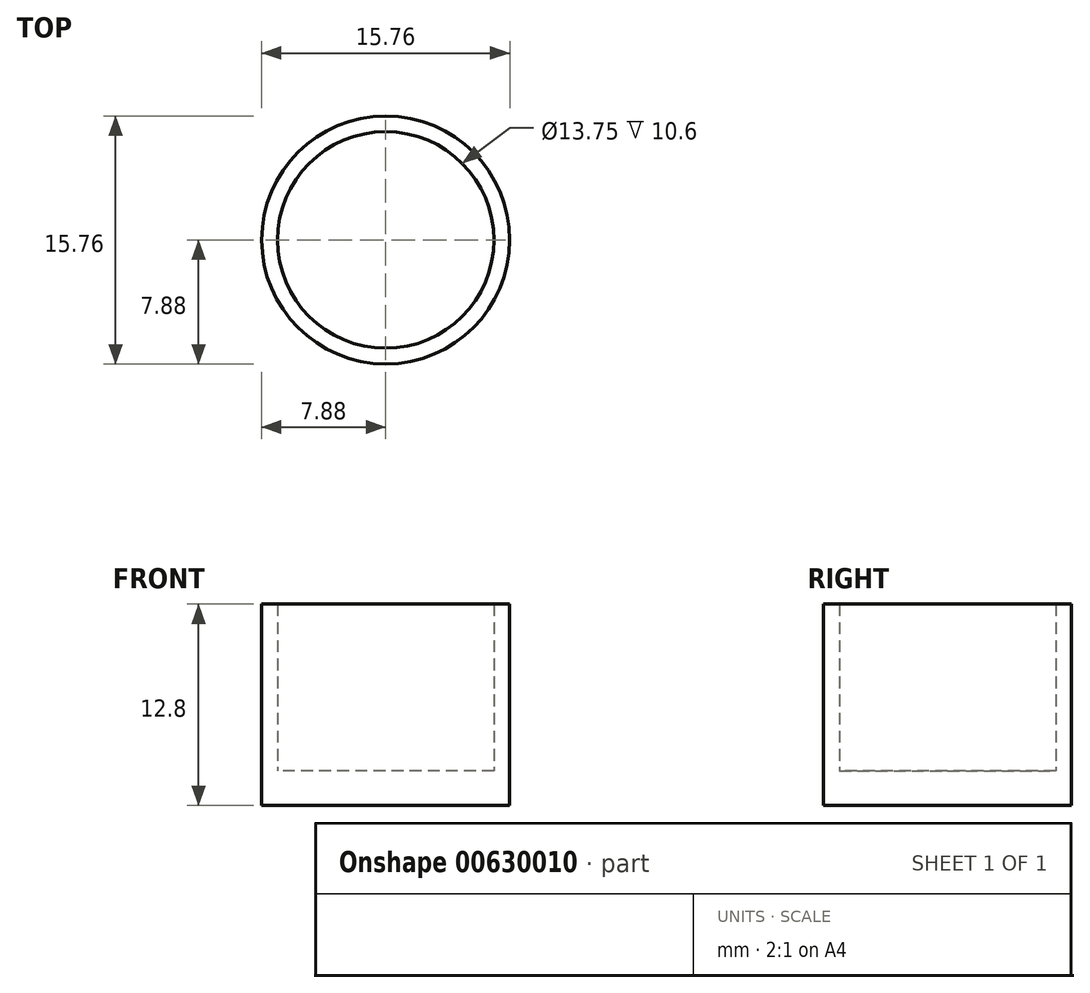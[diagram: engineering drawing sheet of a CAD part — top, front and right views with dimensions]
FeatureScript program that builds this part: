
annotation { "Feature Type Name" : "Feature", "Feature Type Description" : "" }
export const myFeature = defineFeature(function(context is Context, id is Id, definition is map)
    precondition{}
    {
        {
            var Q0;
            Q0=qCreatedBy(makeId("Top.planeOp"),FACE);
            var sketch = newSketch(context, id + "F0", { "sketchPlane" : qUnion([Q0])});
            skCircle(sketch, "E0", {"center": v(0, 0) * mm, "radius": 7.88 * mm});
            skSolve(sketch);
        }
        {
            var Q0;
            Q0=qCreatedBy(makeId("Top.planeOp"),FACE);
            var sketch = newSketch(context, id + "F1", { "sketchPlane" : qUnion([Q0])});
            skCircle(sketch, "E1", {"center": v(0, 0) * mm, "radius": 6.88 * mm});
            skCircle(sketch, "E2", {"center": v(0, 0) * mm, "radius": 7.88 * mm});
            skSolve(sketch);
        }
        {
            var Q0;
            Q0 = qSketchRegion(id + "F0", true);
            extrude(context, id + "F2", {"entities" : qUnion([Q0]), "depth" : 2.2 * mm, "offsetDistance" : 25 * mm});
        }
        {
            var Q0;
            Q0 = qSketchRegion(id + "F1", true);
            extrude(context, id + "F3", {"entities" : qUnion([Q0]), "operationType" : NewBodyOperationType.ADD, "depth" : 12.8 * mm, "offsetDistance" : 25 * mm});
        }
    });
